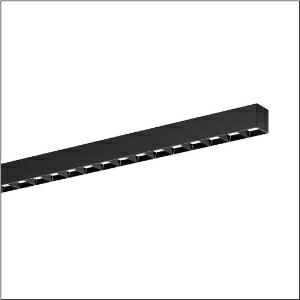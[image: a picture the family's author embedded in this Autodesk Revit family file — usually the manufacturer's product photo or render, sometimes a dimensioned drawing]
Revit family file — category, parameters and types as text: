
# Revit family: silica_r__21_51mx22dc4abb_087a
name_source: partatom
category: Lighting Fixtures
units: mm (PartAtom-declared; Revit-internal decimal feet)

## family parameters
Cut with Voids When Loaded = No
Host = Face
Light Source = No
Part Type = Normal
Room Calculation Point = No
Round Connector Dimension = Use Diameter
Shared = No

## types (1)
- --- (1 x LED, 10800 lm, 64.7 W, 4000K)
    Apparent Load = 65 VA
    CIE Flux Codes = 86 100 100 100 100
    Color Rendering = 80
    Color Temperature = 4000K
    Default Elevation = 1800 mm
    Description = Silica® 21, office luminaire, primary light control with darklight reflector, of PMMA, black, CAT 2 (L<= 3000cd/m²), light emission: direct distribution, primary light characteristic: symmetric, installation type: surface-mounted, LED, rated luminous flux: 10.800lm, luminous efficacy: 167lm/W, light colour: 840, colour temperature: 4000K, with terminal, 3+2-pole, max. 2.5mm², mains connection: 220..240V, AC, 50/60Hz, rated input power: 64.7W, luminaire housing, of aluminium, jet black (RAL 9005), length: 3.004mm, width: 53mm, height: 53mm, protection rating (complete): IP20, insulation class (complete): insulation class I (protective earthing), certification: CE, permissible operating ambient temperature: 0..+35°C, standard: EN 50419, packaging unit: 1 piece
    Height = 0 mm  [stored 0 ft]
    Lamp = 1 x LED
    Lamp Light Flux = 10800 lm
    Lamp Power = 64.7 W
    Lamp count = 1
    Length = 3004 mm
    Luminous efficacy = 167 lm/W
    Manufacturer = Siteco
    ModVariant = No
    Model = 51MX22DC4ABB
    Mounting Place = Ceiling
    Mounting Type = Recessed
    Number of Poles = 1
    OnlyDefault = Yes
    Power Factor = 1
    Product Name = Silica® 21
    Product group = office luminaire | ceiling recessed
    ProductGroupID = 401
    Protection Class = Protection class I
    Protection Degree = IP 20
    RLX_Detail_Level = 1
    RLX_Emergency_Light_Flux = 0 lm
    RLX_Emergency_Type = 0
    RLX_Emergency_Type_DB = No
    RlxData = <blob elided: 64969 chars, md5=6b6c3c77>
    Socket = socket
    Standby Power = 0 W
    System Light Flux = 10800 lm
    System Power = 65 W
    Type Comments = factory setting: luminous flux: 100 % | dim-lin: 254 | 366 mA
    Type Image = l_1297756.jpg
    URL = http://relux.com
    VarID = @adj_056081
    Voltage = 0 V
    Weight = 0.00 kg
    Width = 53 mm

note: [stored X ft] marks values corroborated as IEEE doubles in the binary element streams (Revit-internal decimal feet)

## geometry (parser evidence)
native form markers: Blend x4, Sweep x10
no freeform markers — native parametric forms only
